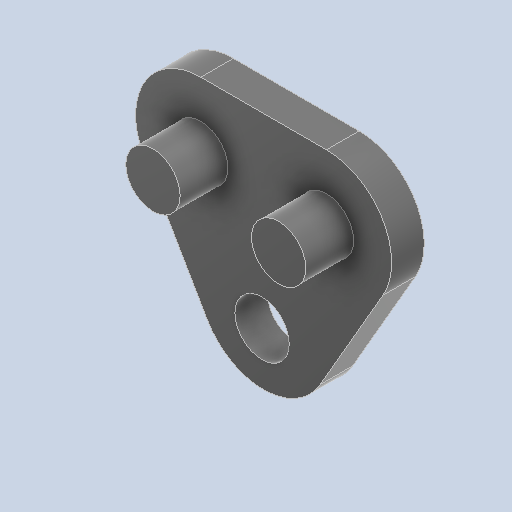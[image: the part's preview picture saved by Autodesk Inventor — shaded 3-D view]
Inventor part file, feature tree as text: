
AUTODESK INVENTOR PART (.ipt)
format: ipt  version: 2022 (Build 260153000, 153)  size: 304,128 bytes
history: native  units: in
note: dims shown in document units (in); Inventor stores cm internally (conversion verified against a paired STEP export)
features: extrude x2, sketch x2, other x1
ambient origin geometry x8: Origin, YZ Plane, XZ Plane, XY Plane, X Axis, Y Axis, Z Axis, Center Point
bodies: Body1 (feature_tree)
feature tree (5):
  other  "Sólido1"
  extrude  "Extrusión1"  Depth=0.0984in
  extrude  "Extrusión2"  Depth=0.0866in
  sketch  "Boceto1"  dims[d2=0.0984in d9=0.0984in]
  sketch  "Boceto3"  dims[d10=0.2496in d13=0.0984in d14=0.2157in d15=0.1228in d16=60.0deg d17=60.0deg d18=60.0deg d19=0.1181in d20=0.0591in d21=0.0in d22=0.0984in d23=0.0984in d24=0.0866in d25=0.0in]
